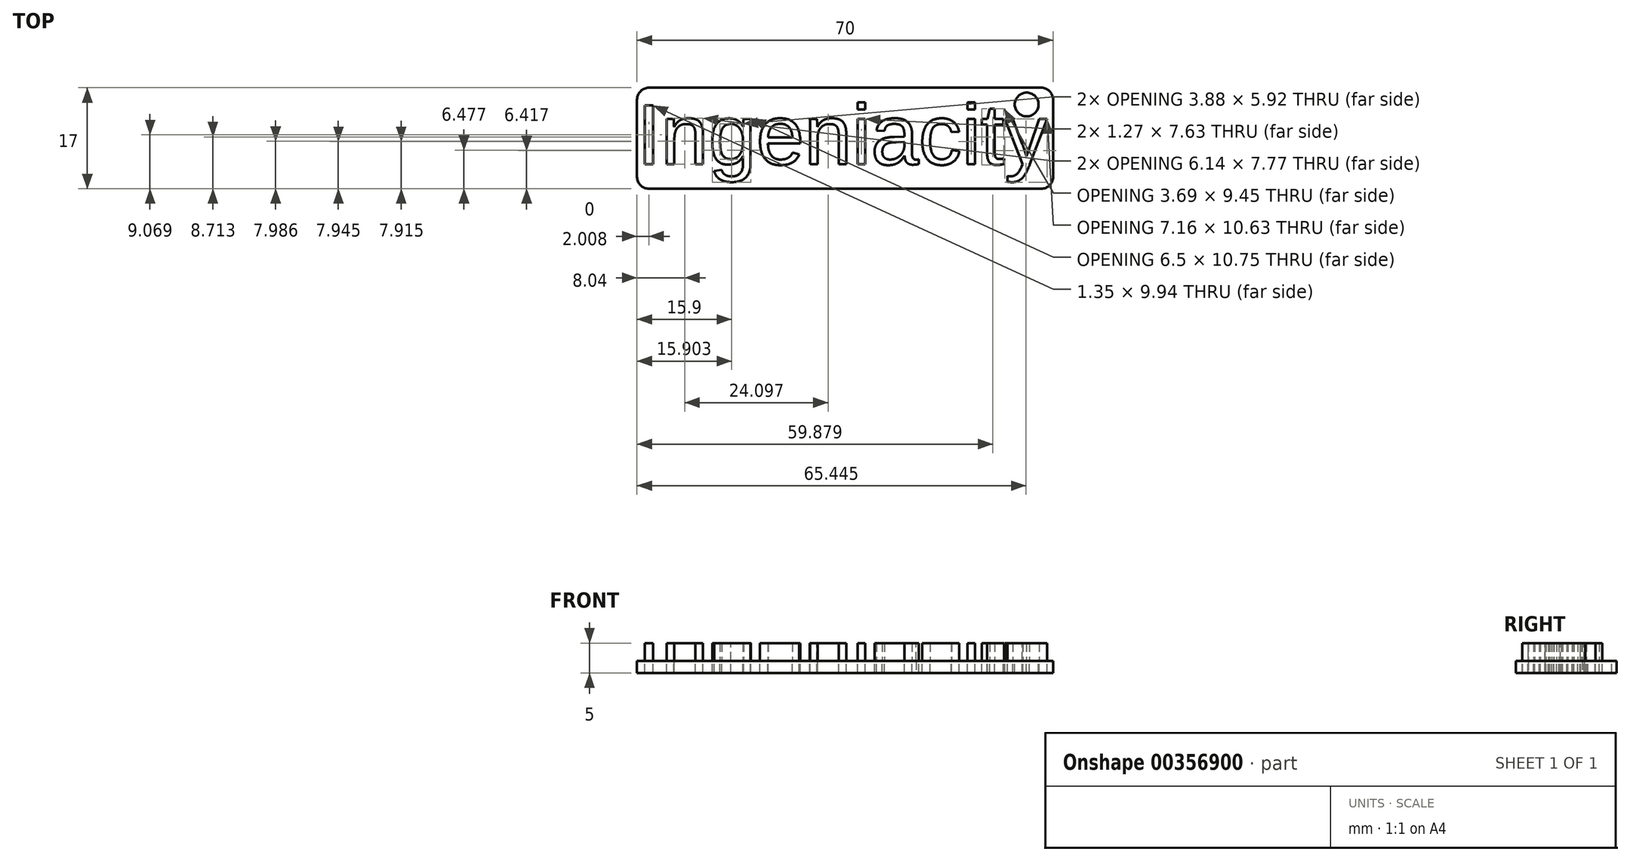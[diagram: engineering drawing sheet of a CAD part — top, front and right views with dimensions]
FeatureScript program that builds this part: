
annotation { "Feature Type Name" : "Feature", "Feature Type Description" : "" }
export const myFeature = defineFeature(function(context is Context, id is Id, definition is map)
    precondition{}
    {
        {
            var Q0;
            Q0=qCreatedBy(makeId("Top.planeOp"),FACE);
            var sketch = newSketch(context, id + "F0", { "sketchPlane" : qUnion([Q0])});
            skLineSegment(sketch, "E0.bottom", {"start": v(2, 0) * mm, "end": v(68, 0) * mm});
            skLineSegment(sketch, "E0.top", {"start": v(2, 17) * mm, "end": v(68, 17) * mm});
            skLineSegment(sketch, "E0.left", {"start": v(0, 2) * mm, "end": v(0, 15) * mm});
            skLineSegment(sketch, "E0.right", {"start": v(70, 2) * mm, "end": v(70, 15) * mm});
            skText(sketch, "E1", { "text": "Ingeniacity", "fontName": "Arimo-Regular.ttf"});
            skPoint(sketch, "E2.visualSharp", {"position": v(0, 17) * mm});
            skArc(sketch, "E2.filletArc", {"start": v(2, 17) * mm, "mid": v(0.59, 16.41) * mm, "end": v(0, 15) * mm});
            skPoint(sketch, "E3.visualSharp", {"position": v(0, 0) * mm});
            skArc(sketch, "E3.filletArc", {"start": v(0, 2) * mm, "mid": v(0.59, 0.59) * mm, "end": v(2, 0) * mm});
            skPoint(sketch, "E4.visualSharp", {"position": v(70, 17) * mm});
            skArc(sketch, "E4.filletArc", {"start": v(70, 15) * mm, "mid": v(69.41, 16.41) * mm, "end": v(68, 17) * mm});
            skPoint(sketch, "E5.visualSharp", {"position": v(70, 0) * mm});
            skArc(sketch, "E5.filletArc", {"start": v(68, 0) * mm, "mid": v(69.41, 0.59) * mm, "end": v(70, 2) * mm});
            skCircle(sketch, "E6", {"center": v(65.55, 14.18) * mm, "radius": 2 * mm});
            const initialGuessF0  = {"E1": [0, 0.0041, 1, 0, 0.0104]};
            skSetInitialGuess(sketch, initialGuessF0);
            skSolve(sketch);
        }
        {
            var Q0;
            Q0=makeQuery(id+"F0.imprint","IMPRINT",FACE,{"disambiguationData":[TD([[makeQuery(id+"F0.imprint","IMPRINT",EDGE,{"derivedFrom":sQuery(id+"F0.wireOp",EDGE,"E1.sketch_text.stroke-0")}),-1.0]])]});
            var Q1;
            Q1=makeQuery(id+"F0.imprint","IMPRINT",FACE,{"disambiguationData":[TD([[makeQuery(id+"F0.imprint","IMPRINT",EDGE,{"derivedFrom":sQuery(id+"F0.wireOp",EDGE,"E1.sketch_text.stroke-4")}),-1.0]])]});
            var Q2;
            Q2=makeQuery(id+"F0.imprint","IMPRINT",FACE,{"disambiguationData":[TD([[makeQuery(id+"F0.imprint","IMPRINT",EDGE,{"derivedFrom":sQuery(id+"F0.wireOp",EDGE,"E1.sketch_text.stroke-25")}),-1.0]])]});
            var Q3;
            Q3=makeQuery(id+"F0.imprint","IMPRINT",FACE,{"disambiguationData":[TD([[makeQuery(id+"F0.imprint","IMPRINT",EDGE,{"derivedFrom":sQuery(id+"F0.wireOp",EDGE,"E1.sketch_text.stroke-58")}),-1.0]])]});
            var Q4;
            Q4=makeQuery(id+"F0.imprint","IMPRINT",FACE,{"disambiguationData":[TD([[makeQuery(id+"F0.imprint","IMPRINT",EDGE,{"derivedFrom":sQuery(id+"F0.wireOp",EDGE,"E1.sketch_text.stroke-76")}),-1.0]])]});
            var Q5;
            Q5=makeQuery(id+"F0.imprint","IMPRINT",FACE,{"disambiguationData":[TD([[makeQuery(id+"F0.imprint","IMPRINT",EDGE,{"derivedFrom":sQuery(id+"F0.wireOp",EDGE,"E1.sketch_text.stroke-101")}),-1.0]])]});
            var Q6;
            Q6=makeQuery(id+"F0.imprint","IMPRINT",FACE,{"disambiguationData":[TD([[makeQuery(id+"F0.imprint","IMPRINT",EDGE,{"derivedFrom":sQuery(id+"F0.wireOp",EDGE,"E1.sketch_text.stroke-105")}),-1.0]])]});
            var Q7;
            Q7=makeQuery(id+"F0.imprint","IMPRINT",FACE,{"disambiguationData":[TD([[makeQuery(id+"F0.imprint","IMPRINT",EDGE,{"derivedFrom":sQuery(id+"F0.wireOp",EDGE,"E1.sketch_text.stroke-140")}),-1.0]])]});
            var Q8;
            Q8=makeQuery(id+"F0.imprint","IMPRINT",FACE,{"disambiguationData":[TD([[makeQuery(id+"F0.imprint","IMPRINT",EDGE,{"derivedFrom":sQuery(id+"F0.wireOp",EDGE,"E1.sketch_text.stroke-166")}),-1.0]])]});
            var Q9;
            Q9=makeQuery(id+"F0.imprint","IMPRINT",FACE,{"disambiguationData":[TD([[makeQuery(id+"F0.imprint","IMPRINT",EDGE,{"derivedFrom":sQuery(id+"F0.wireOp",EDGE,"E1.sketch_text.stroke-183")}),-1.0]])]});
            var Q10;
            Q10=makeQuery(id+"F0.imprint","IMPRINT",FACE,{"disambiguationData":[TD([[makeQuery(id+"F0.imprint","IMPRINT",EDGE,{"derivedFrom":sQuery(id+"F0.wireOp",EDGE,"E1.sketch_text.stroke-162")}),-1.0]])]});
            var Q11;
            Q11=makeQuery(id+"F0.imprint","IMPRINT",FACE,{"disambiguationData":[TD([[makeQuery(id+"F0.imprint","IMPRINT",EDGE,{"derivedFrom":sQuery(id+"F0.wireOp",EDGE,"E1.sketch_text.stroke-158")}),-1.0]])]});
            var Q12;
            Q12=makeQuery(id+"F0.imprint","IMPRINT",FACE,{"disambiguationData":[TD([[makeQuery(id+"F0.imprint","IMPRINT",EDGE,{"derivedFrom":sQuery(id+"F0.wireOp",EDGE,"E1.sketch_text.stroke-97")}),-1.0]])]});
            extrude(context, id + "F1", {"entities" : qUnion([Q0, Q1, Q2, Q3, Q4, Q5, Q6, Q7, Q8, Q9, Q10, Q11, Q12]), "depth" : 3 * mm, "offsetDistance" : 25 * mm});
        }
        {
            var Q0;
            Q0=makeQuery(id+"F0.imprint","IMPRINT",FACE,{"disambiguationData":[TD([[makeQuery(id+"F0.imprint","IMPRINT",EDGE,{"derivedFrom":sQuery(id+"F0.wireOp",EDGE,"E0.bottom")}),1.0]])]});
            extrude(context, id + "F2", {"entities" : qUnion([Q0]), "oppositeDirection" : true, "depth" : 2 * mm, "offsetDistance" : 25 * mm});
        }
        {
            var Q0;
            Q0=makeQuery(id+"F0.imprint","IMPRINT",FACE,{"disambiguationData":[TD([[makeQuery(id+"F0.imprint","IMPRINT",EDGE,{"derivedFrom":sQuery(id+"F0.wireOp",EDGE,"E1.sketch_text.stroke-0")}),-1.0]])]});
            var Q1;
            Q1=makeQuery(id+"F0.imprint","IMPRINT",FACE,{"disambiguationData":[TD([[makeQuery(id+"F0.imprint","IMPRINT",EDGE,{"derivedFrom":sQuery(id+"F0.wireOp",EDGE,"E1.sketch_text.stroke-4")}),-1.0]])]});
            var Q2;
            Q2=makeQuery(id+"F0.imprint","IMPRINT",FACE,{"disambiguationData":[TD([[makeQuery(id+"F0.imprint","IMPRINT",EDGE,{"derivedFrom":sQuery(id+"F0.wireOp",EDGE,"E1.sketch_text.stroke-25")}),-1.0]])]});
            var Q3;
            Q3=makeQuery(id+"F0.imprint","IMPRINT",FACE,{"disambiguationData":[TD([[makeQuery(id+"F0.imprint","IMPRINT",EDGE,{"derivedFrom":sQuery(id+"F0.wireOp",EDGE,"E1.sketch_text.stroke-58")}),-1.0]])]});
            var Q4;
            Q4=makeQuery(id+"F0.imprint","IMPRINT",FACE,{"disambiguationData":[TD([[makeQuery(id+"F0.imprint","IMPRINT",EDGE,{"derivedFrom":sQuery(id+"F0.wireOp",EDGE,"E1.sketch_text.stroke-76")}),-1.0]])]});
            var Q5;
            Q5=makeQuery(id+"F0.imprint","IMPRINT",FACE,{"disambiguationData":[TD([[makeQuery(id+"F0.imprint","IMPRINT",EDGE,{"derivedFrom":sQuery(id+"F0.wireOp",EDGE,"E1.sketch_text.stroke-101")}),-1.0]])]});
            var Q6;
            Q6=makeQuery(id+"F0.imprint","IMPRINT",FACE,{"disambiguationData":[TD([[makeQuery(id+"F0.imprint","IMPRINT",EDGE,{"derivedFrom":sQuery(id+"F0.wireOp",EDGE,"E1.sketch_text.stroke-105")}),-1.0]])]});
            var Q7;
            Q7=makeQuery(id+"F0.imprint","IMPRINT",FACE,{"disambiguationData":[TD([[makeQuery(id+"F0.imprint","IMPRINT",EDGE,{"derivedFrom":sQuery(id+"F0.wireOp",EDGE,"E1.sketch_text.stroke-97")}),-1.0]])]});
            var Q8;
            Q8=makeQuery(id+"F0.imprint","IMPRINT",FACE,{"disambiguationData":[TD([[makeQuery(id+"F0.imprint","IMPRINT",EDGE,{"derivedFrom":sQuery(id+"F0.wireOp",EDGE,"E1.sketch_text.stroke-140")}),-1.0]])]});
            var Q9;
            Q9=makeQuery(id+"F0.imprint","IMPRINT",FACE,{"disambiguationData":[TD([[makeQuery(id+"F0.imprint","IMPRINT",EDGE,{"derivedFrom":sQuery(id+"F0.wireOp",EDGE,"E1.sketch_text.stroke-162")}),-1.0]])]});
            var Q10;
            Q10=makeQuery(id+"F0.imprint","IMPRINT",FACE,{"disambiguationData":[TD([[makeQuery(id+"F0.imprint","IMPRINT",EDGE,{"derivedFrom":sQuery(id+"F0.wireOp",EDGE,"E1.sketch_text.stroke-183")}),-1.0]])]});
            var Q11;
            Q11=makeQuery(id+"F0.imprint","IMPRINT",FACE,{"disambiguationData":[TD([[makeQuery(id+"F0.imprint","IMPRINT",EDGE,{"derivedFrom":sQuery(id+"F0.wireOp",EDGE,"E1.sketch_text.stroke-158")}),-1.0]])]});
            var Q12;
            Q12=makeQuery(id+"F0.imprint","IMPRINT",FACE,{"disambiguationData":[TD([[makeQuery(id+"F0.imprint","IMPRINT",EDGE,{"derivedFrom":sQuery(id+"F0.wireOp",EDGE,"E1.sketch_text.stroke-166")}),-1.0]])]});
            extrude(context, id + "F3", {"entities" : qUnion([Q0, Q1, Q2, Q3, Q4, Q5, Q6, Q7, Q8, Q9, Q10, Q11, Q12]), "oppositeDirection" : true, "depth" : 2 * mm, "offsetDistance" : 25 * mm});
        }
    });
